# Revit family: Precast Slab-Hollow Core-Top
name_source: partatom
category: Detail Items
revit_build: Autodesk Revit Architecture 2012 (Build: 20110210_1515)
units: mm (PartAtom-declared; Revit-internal decimal feet)

## types (12) — shared parameters
Width = 4' - 0"

## per-type parameters (varying)
| type | Core Offset | Core Radius | Depth | Keynote | Number Of Cores |
| 4HC6 | 0' - 3" | 0' - 2" | 0' - 6" | 03 41 00.C1 | 8 |
| 4HC6+2 | 0' - 3" | 0' - 2" | 0' - 6" | 03 41 00.C2 | 8 |
| 4HC8 | 0' - 4" | 0' - 2 11/16" | 0' - 8" | 03 41 00.C3 | 6 |
| 4HC8+2 | 0' - 4" | 0' - 2 11/16" | 0' - 8" | 03 41 00.C4 | 6 |
| 4LHC8+2 | 0' - 4" | 0' - 2 11/16" | 0' - 8" | 03 41 00.C6 | 6 |
| 4LHC8 | 0' - 4" | 0' - 2 11/16" | 0' - 8" | 03 41 00.C5 | 6 |
| 4HC10 | 0' - 9" | 0' - 3 5/16" | 0' - 10" | 03 41 00.C7 | 4 |
| 4HC10+2 | 0' - 9" | 0' - 3 5/16" | 0' - 10" | 03 41 00.C8 | 4 |
| 4HC12 | 0' - 6" | 0' - 4" | 1' - 0" | 03 41 00.C9 | 4 |
| 4HC12+2 | 0' - 6" | 0' - 4" | 1' - 0" | 03 41 00.C10 | 4 |
| 4LHC12 | 0' - 6" | 0' - 4" | 1' - 0" | 03 41 00.C11 | 4 |
| 4LHC12+2 | 0' - 6" | 0' - 4" | 1' - 0" | 03 41 00.C12 | 4 |

## geometry (parser evidence)
native form markers: Sweep x2
no freeform markers — native parametric forms only
